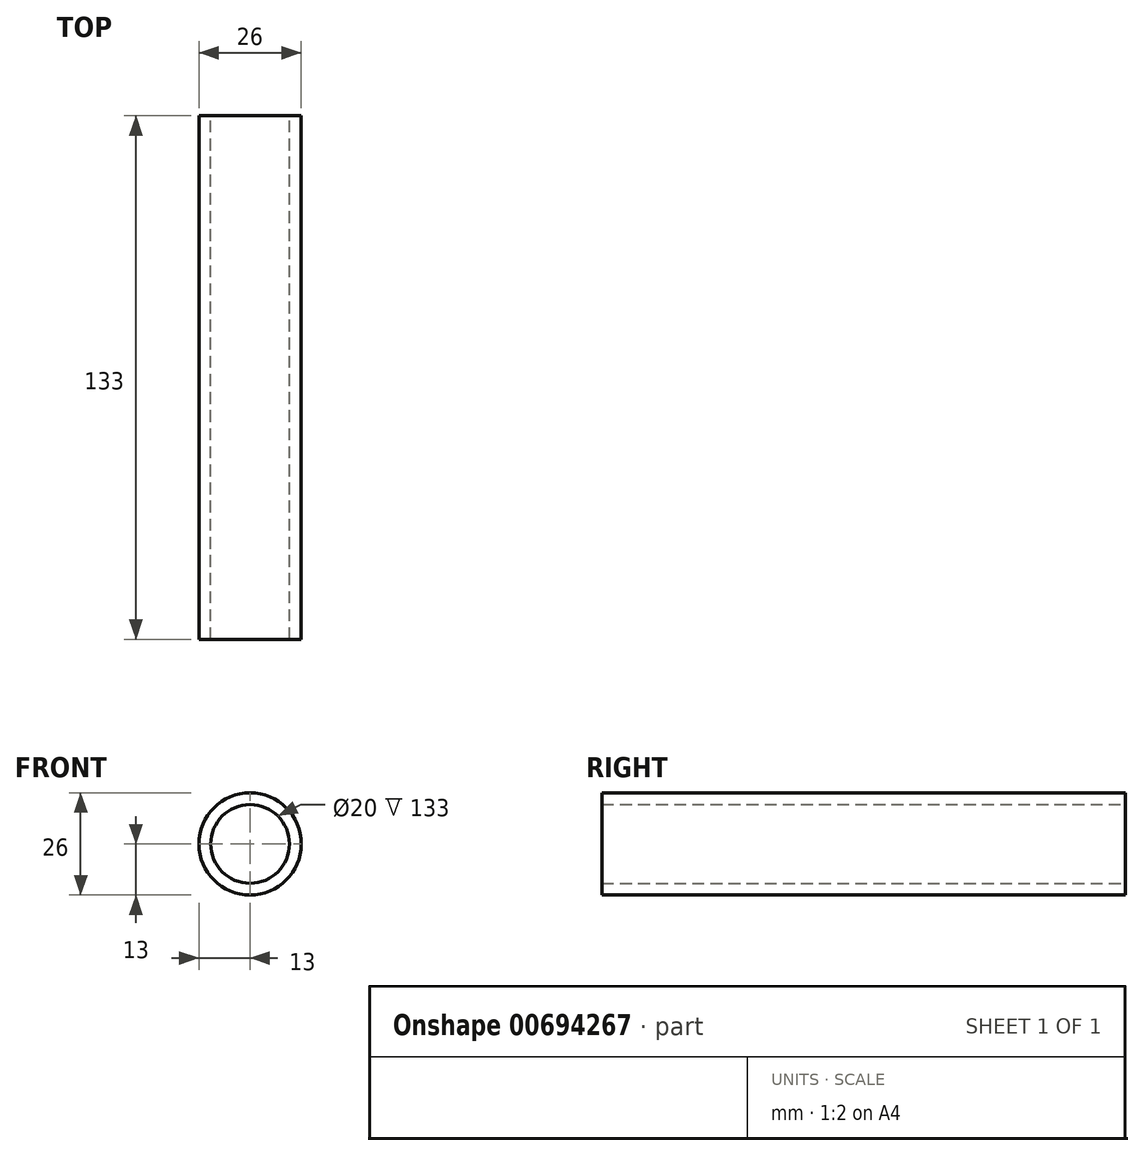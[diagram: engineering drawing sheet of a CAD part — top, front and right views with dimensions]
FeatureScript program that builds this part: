
annotation { "Feature Type Name" : "Feature", "Feature Type Description" : "" }
export const myFeature = defineFeature(function(context is Context, id is Id, definition is map)
    precondition{}
    {
        {
            var Q0;
            Q0=qCreatedBy(makeId("Front.planeOp"),FACE);
            var sketch = newSketch(context, id + "F0", { "sketchPlane" : qUnion([Q0])});
            skCircle(sketch, "E0", {"center": v(0, 0) * mm, "radius": 10 * mm});
            skCircle(sketch, "E1", {"center": v(0, 0) * mm, "radius": 13 * mm});
            skSolve(sketch);
        }
        {
            var Q0;
            Q0=qSketchRegion(id+"F0",true);
            extrude(context, id + "F1", {"entities" : qUnion([Q0]), "depth" : 133 * mm, "offsetDistance" : 25 * mm});
        }
    });
